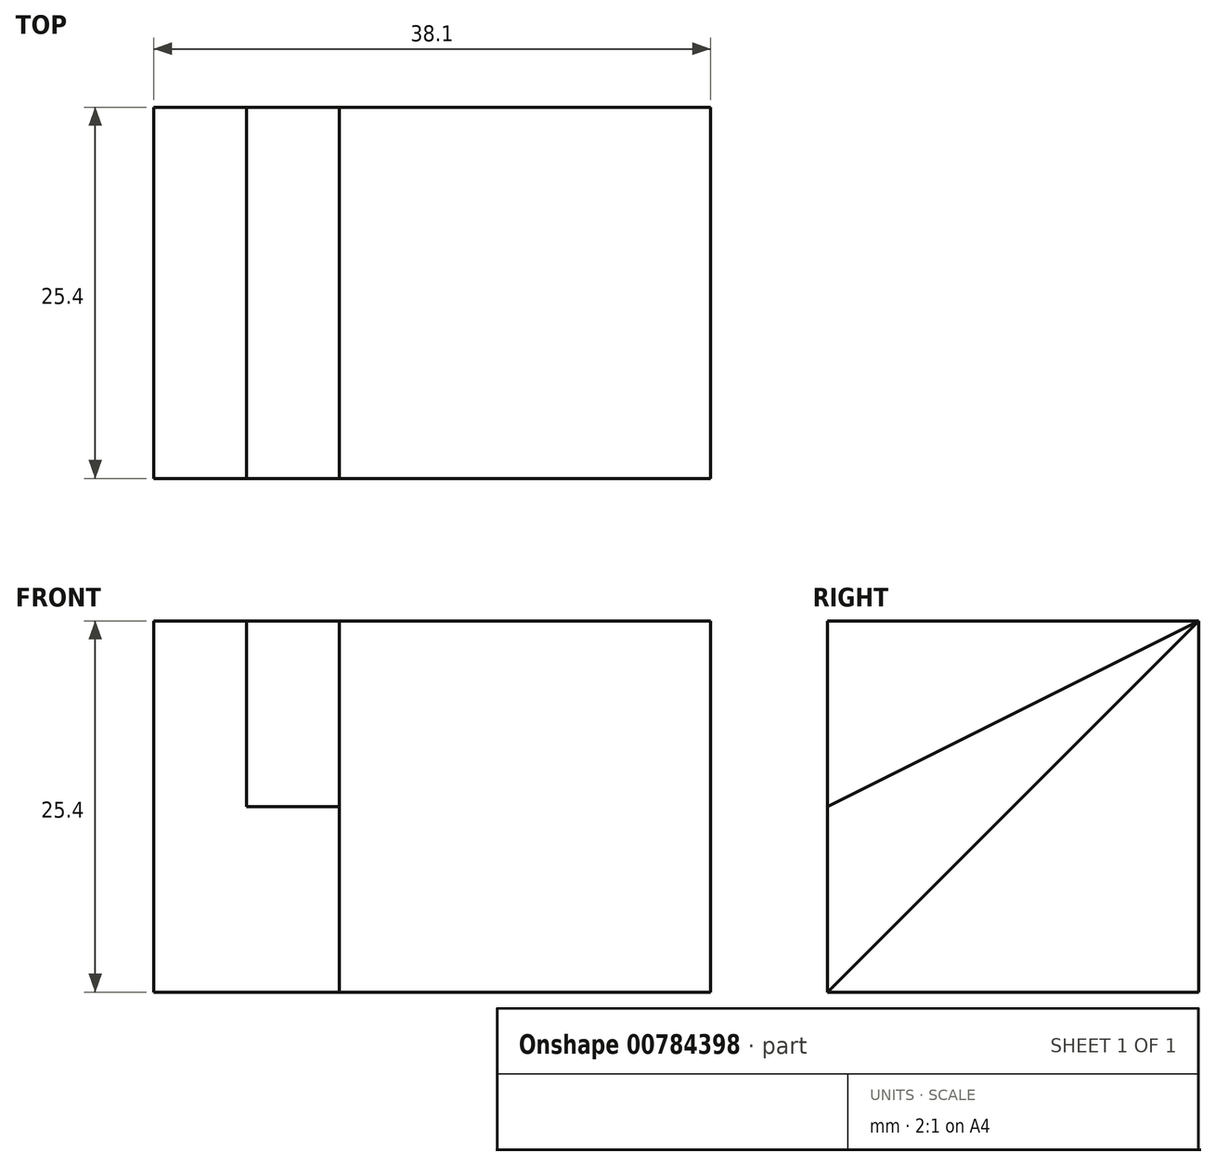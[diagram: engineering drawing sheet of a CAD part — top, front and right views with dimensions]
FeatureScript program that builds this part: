
annotation { "Feature Type Name" : "Feature", "Feature Type Description" : "" }
export const myFeature = defineFeature(function(context is Context, id is Id, definition is map)
    precondition{}
    {
        {
            var Q0;
            Q0=qCreatedBy(makeId("Front.planeOp"),FACE);
            var sketch = newSketch(context, id + "F0", { "sketchPlane" : qUnion([Q0])});
            skLineSegment(sketch, "E0", {"start": v(0, 0) * mm, "end": v(38.1, 0) * mm});
            skLineSegment(sketch, "E1", {"start": v(38.1, 0) * mm, "end": v(38.1, 25.4) * mm});
            skLineSegment(sketch, "E2", {"start": v(38.1, 25.4) * mm, "end": v(0, 25.4) * mm});
            skLineSegment(sketch, "E3", {"start": v(0, 25.4) * mm, "end": v(0, 0) * mm});
            skSolve(sketch);
        }
        {
            var Q0;
            Q0 = qSketchRegion(id + "F0", true);
            extrude(context, id + "F1", {"entities" : qUnion([Q0]), "depth" : 25.4 * mm, "offsetDistance" : 25.4 * mm});
        }
        {
            var Q0;
            Q0=makeQuery(id+"F1.opExtrude","SWEPT_FACE",FACE,{"disambiguationData":[OSD([sQuery(id+"F0.wireOp",EDGE,"E1")])]});
            var sketch = newSketch(context, id + "F2", { "sketchPlane" : qUnion([Q0])});
            skLineSegment(sketch, "E4", {"start": v(0, 25.4) * mm, "end": v(-25.4, 0) * mm});
            skLineSegment(sketch, "E5", {"start": v(-25.4, 0) * mm, "end": v(-25.4, 25.4) * mm});
            skLineSegment(sketch, "E6", {"start": v(-25.4, 25.4) * mm, "end": v(0, 25.4) * mm});
            skSolve(sketch);
        }
        {
            var Q0;
            Q0=makeQuery(id+"F2.imprint","IMPRINT",FACE,{"disambiguationData":[TD([[makeQuery(id+"F2.imprint","IMPRINT",EDGE,{"derivedFrom":sQuery(id+"F2.wireOp",EDGE,"E4")}),-1.0]])]});
            extrude(context, id + "F3", {"entities" : qUnion([Q0]), "operationType" : NewBodyOperationType.REMOVE, "oppositeDirection" : true, "depth" : 25.4 * mm, "offsetDistance" : 25.4 * mm});
        }
        {
            var Q0;
            Q0=makeQuery(id+"F3.boolean.opBoolean","COPY",FACE,{"derivedFrom":makeQuery(id+"F3.opExtrude","CAP_FACE",FACE,{"disambiguationData":[OSD([sQuery(id+"F2.wireOp",EDGE,"E4"),sQuery(id+"F2.wireOp",EDGE,"E5"),sQuery(id+"F2.wireOp",EDGE,"E6")])],"isStart":false})});
            var sketch = newSketch(context, id + "F4", { "sketchPlane" : qUnion([Q0])});
            skLineSegment(sketch, "E7", {"start": v(-25.4, 0) * mm, "end": v(-25.4, 12.7) * mm});
            skLineSegment(sketch, "E8", {"start": v(-25.4, 12.7) * mm, "end": v(0, 25.4) * mm});
            skLineSegment(sketch, "E9", {"start": v(0, 25.4) * mm, "end": v(-25.4, 25.4) * mm});
            skLineSegment(sketch, "E10", {"start": v(-25.4, 25.4) * mm, "end": v(-25.4, 12.7) * mm});
            skSolve(sketch);
        }
        {
            var Q0;
            Q0=makeQuery(id+"F4.imprint","IMPRINT",FACE,{"disambiguationData":[TD([[makeQuery(id+"F4.imprint","IMPRINT",EDGE,{"derivedFrom":sQuery(id+"F4.wireOp",EDGE,"E8")}),1.0]])]});
            extrude(context, id + "F5", {"entities" : qUnion([Q0]), "operationType" : NewBodyOperationType.REMOVE, "oppositeDirection" : true, "depth" : 6.35 * mm, "offsetDistance" : 25.4 * mm});
        }
    });
